# Revit family: Flushometer-Manual_Specialty-Sloan-Royal-952_Series
name_source: partatom
category: Plumbing Fixtures
revit_build: Autodesk Revit 2016 (Build: 20150714_1515(x64)
units: mm (PartAtom-declared; Revit-internal decimal feet)

## family parameters
Always vertical = No
Cut with Voids When Loaded = No
OmniClass Number = 23.65.00.00
OmniClass Title = Supply and Distribution of Liquids and Gases
Part Type = Normal
Room Calculation Point = No
Round Connector Dimension = Use Diameter
Shared = Yes
Work Plane-Based = Yes

## types (3) — shared parameters
ADA Compliant = Yes
Assembly Code = D2020
Buy American Act Compliant = Yes
CW Connection = Yes
CWFU = 10
Default Elevation = 0"
Finish(es) = RB
Fixture Color = Not Applicable
Flush Choice = Single Flush
HW Connection = No
IAPMO Certification = UPC
Inlet Spud Size = 1" IPS
Manufacturer = SLOAN
Material = Semi-red Brass
Mounting = Concealed
Operation = Hydraulic
Price = Prices may vary. Please consult Sloan Rep for most up-to-date price list.
Product URL = https://www.sloan.com
Spud Location = Rear Spud
URL = www.sloan.com
Vent Connection = No
WFU = 10
Warranty = 3 Year (Limited)
Waste Connection = No
zero-valued in all types: HWFU

## per-type parameters (varying)
| type | Description | Flush Volume(s)/Flow Rate(s) | High-Efficiency |
| Royal 952-1.6 | Concealed, Royal® hydraulically-activated water closet flushometer, for wall hung rear spud bowls. | 1.6 gpf (6.0 Lpf) | No |
| Royal 952-3.5 | Concealed, Royal® hydraulically-activated water closet flushometer, for wall hung rear spud bowls. | 3.5 gpf (13.2 Lpf) | No |
| Royal 952-1.28 | Concealed, Royal® hydraulically-activated high-efficiency water closet flushometer, for high-efficiency wall hung rear spud bowls. | 1.28 gpf (4.8 Lpf) | Yes |

note: column(s) folded — value = type name in every type: Model

## geometry (parser evidence)
native form markers: Sweep x2
no freeform markers — native parametric forms only
